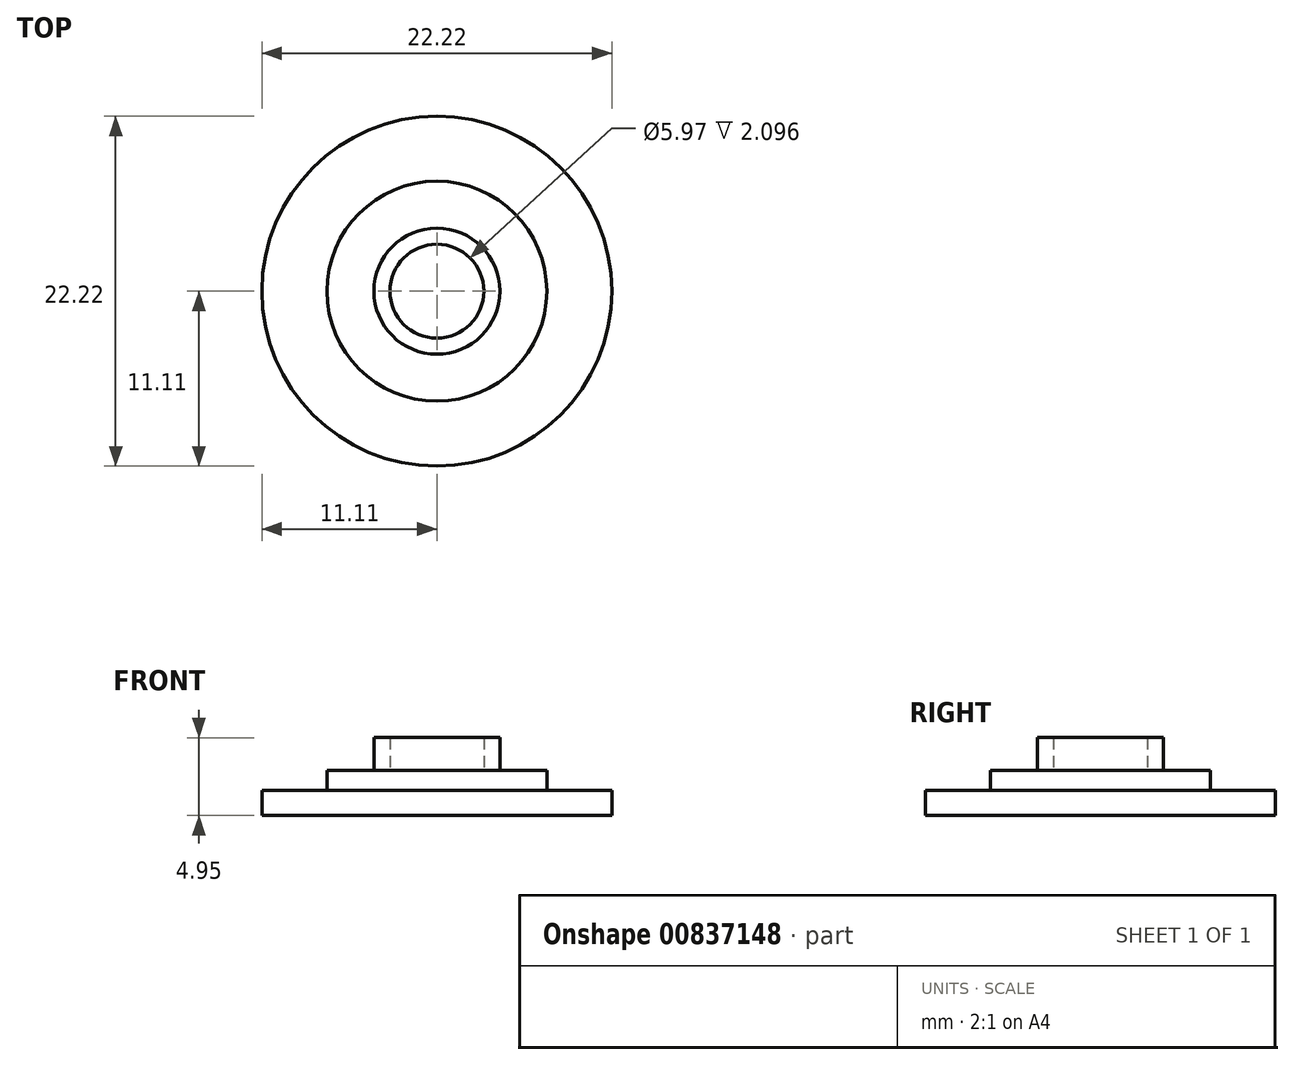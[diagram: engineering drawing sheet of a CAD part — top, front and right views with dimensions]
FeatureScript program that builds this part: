
annotation { "Feature Type Name" : "Feature", "Feature Type Description" : "" }
export const myFeature = defineFeature(function(context is Context, id is Id, definition is map)
    precondition{}
    {
        {
            var Q0;
            Q0=qCreatedBy(makeId("Top.planeOp"),FACE);
            var sketch = newSketch(context, id + "F0", { "sketchPlane" : qUnion([Q0])});
            skCircle(sketch, "E0", {"center": v(0, 0) * mm, "radius": 11.11 * mm});
            skSolve(sketch);
        }
        {
            var Q0;
            Q0=makeQuery(id+"F0.imprint","IMPRINT",FACE,{"disambiguationData":[TD([[makeQuery(id+"F0.imprint","IMPRINT",EDGE,{"derivedFrom":sQuery(id+"F0.wireOp",EDGE,"E0")}),1.0]])]});
            extrude(context, id + "F1", {"entities" : qUnion([Q0]), "depth" : 1.59 * mm, "offsetDistance" : 25.4 * mm});
        }
        {
            var Q0;
            Q0=makeQuery(id+"F1.opExtrude","CAP_FACE",FACE,{"disambiguationData":[OSD([sQuery(id+"F0.wireOp",EDGE,"E0")])],"isStart":false});
            var sketch = newSketch(context, id + "F2", { "sketchPlane" : qUnion([Q0])});
            skCircle(sketch, "E1", {"center": v(0, 0) * mm, "radius": 6.99 * mm});
            skSolve(sketch);
        }
        {
            var Q0;
            Q0=makeQuery(id+"F2.imprint","IMPRINT",FACE,{"disambiguationData":[TD([[makeQuery(id+"F2.imprint","IMPRINT",EDGE,{"derivedFrom":sQuery(id+"F2.wireOp",EDGE,"E1")}),1.0]])]});
            extrude(context, id + "F3", {"entities" : qUnion([Q0]), "operationType" : NewBodyOperationType.ADD, "depth" : 1.27 * mm, "offsetDistance" : 25.4 * mm});
        }
        {
            var Q0;
            Q0=makeQuery(id+"F3.opExtrude","CAP_FACE",FACE,{"disambiguationData":[OSD([sQuery(id+"F2.wireOp",EDGE,"E1")])],"isStart":false});
            var sketch = newSketch(context, id + "F4", { "sketchPlane" : qUnion([Q0])});
            skCircle(sketch, "E2", {"center": v(0, 0) * mm, "radius": 4 * mm});
            skCircle(sketch, "E3.0", {"center": v(0, 0) * mm, "radius": 2.98 * mm});
            skSolve(sketch);
        }
        {
            var Q0;
            Q0=makeQuery(id+"F4.imprint","IMPRINT",FACE,{"disambiguationData":[TD([[makeQuery(id+"F4.imprint","IMPRINT",EDGE,{"derivedFrom":sQuery(id+"F4.wireOp",EDGE,"E2")}),1.0]])]});
            extrude(context, id + "F5", {"entities" : qUnion([Q0]), "operationType" : NewBodyOperationType.ADD, "depth" : 2.1 * mm, "offsetDistance" : 25.4 * mm});
        }
    });
